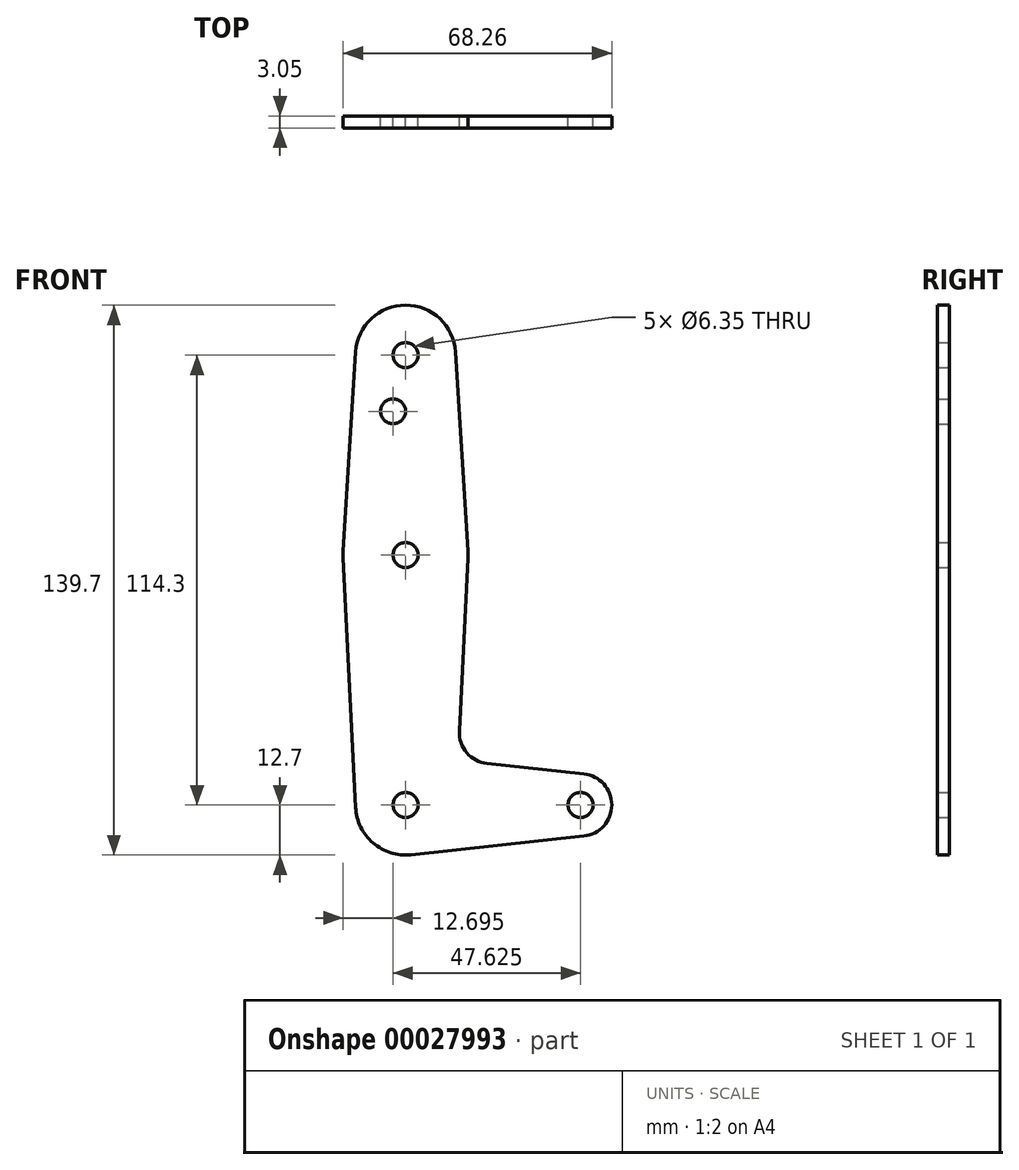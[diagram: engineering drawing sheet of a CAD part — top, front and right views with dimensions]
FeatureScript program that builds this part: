
annotation { "Feature Type Name" : "Feature", "Feature Type Description" : "" }
export const myFeature = defineFeature(function(context is Context, id is Id, definition is map)
    precondition{}
    {
        {
            var Q0;
            Q0=qCreatedBy(makeId("Front.planeOp"),FACE);
            var sketch = newSketch(context, id + "F0", { "sketchPlane" : qUnion([Q0])});
            skLineSegment(sketch, "E0", {"start": v(0, 0) * mm, "end": v(0, 114.3) * mm, "construction": true});
            skLineSegment(sketch, "E1", {"start": v(0, 0) * mm, "end": v(44.45, 0) * mm, "construction": true});
            skCircle(sketch, "E2", {"center": v(0, 0) * mm, "radius": 12.7 * mm});
            skCircle(sketch, "E3", {"center": v(44.45, 0) * mm, "radius": 7.94 * mm});
            skCircle(sketch, "E4", {"center": v(0, 114.3) * mm, "radius": 12.7 * mm});
            skCircle(sketch, "E5", {"center": v(0, 63.5) * mm, "radius": 15.88 * mm});
            skLineSegment(sketch, "E6", {"start": v(-12.68, 115.1) * mm, "end": v(-15.84, 64.5) * mm});
            skLineSegment(sketch, "E7", {"start": v(-15.86, 62.7) * mm, "end": v(-12.68, -0.63) * mm});
            skLineSegment(sketch, "E8", {"start": v(12.68, 115.1) * mm, "end": v(15.84, 64.5) * mm});
            skLineSegment(sketch, "E9", {"start": v(15.86, 62.7) * mm, "end": v(13.66, 18.84) * mm});
            skLineSegment(sketch, "E10", {"start": v(20.75, 10.54) * mm, "end": v(45.3, 7.9) * mm});
            skLineSegment(sketch, "E11", {"start": v(1.36, -12.63) * mm, "end": v(45.3, -7.9) * mm});
            skCircle(sketch, "E12", {"center": v(0, 114.3) * mm, "radius": 3.18 * mm});
            skCircle(sketch, "E13", {"center": v(0, 63.5) * mm, "radius": 3.18 * mm});
            skCircle(sketch, "E14", {"center": v(0, 0) * mm, "radius": 3.18 * mm});
            skCircle(sketch, "E15", {"center": v(44.45, 0) * mm, "radius": 3.18 * mm});
            skCircle(sketch, "E16", {"center": v(-3.18, 100.03) * mm, "radius": 3.18 * mm});
            skArc(sketch, "E17.filletArc", {"start": v(13.66, 18.84) * mm, "mid": v(15.55, 13.28) * mm, "end": v(20.75, 10.54) * mm});
            skSolve(sketch);
        }
        {
            var Q0;
            Q0=makeQuery(id+"F0.imprint","IMPRINT",FACE,{"disambiguationData":[TD([[makeQuery(id+"F0.imprint","IMPRINT",EDGE,{"derivedFrom":sQuery(id+"F0.wireOp",EDGE,"E14")}),-1.0]])]});
            var Q1;
            Q1=makeQuery(id+"F0.imprint","IMPRINT",FACE,{"disambiguationData":[TD([[makeQuery(id+"F0.imprint","IMPRINT",EDGE,{"derivedFrom":sQuery(id+"F0.wireOp",EDGE,"E15")}),-1.0]])]});
            var Q2;
            {var subQ2=sQuery(id+"F0.wireOp",EDGE,"E7");Q2=makeQuery(id+"F0.imprint","IMPRINT",FACE,{"disambiguationData":[TD([[makeQuery(id+"F0.imprint","IMPRINT",EDGE,{"derivedFrom":subQ2}),1.0]])]});}
            var Q3;
            Q3=makeQuery(id+"F0.imprint","IMPRINT",FACE,{"disambiguationData":[TD([[makeQuery(id+"F0.imprint","IMPRINT",EDGE,{"derivedFrom":sQuery(id+"F0.wireOp",EDGE,"E12")}),-1.0]])]});
            var Q4;
            {var subQ1=sQuery(id+"F0.wireOp",EDGE,"E6");Q4=makeQuery(id+"F0.imprint","IMPRINT",FACE,{"disambiguationData":[TD([[makeQuery(id+"F0.imprint","IMPRINT",EDGE,{"derivedFrom":subQ1}),1.0]])]});}
            var Q5;
            Q5=makeQuery(id+"F0.imprint","IMPRINT",FACE,{"disambiguationData":[TD([[makeQuery(id+"F0.imprint","IMPRINT",EDGE,{"derivedFrom":sQuery(id+"F0.wireOp",EDGE,"E13")}),-1.0]])]});
            extrude(context, id + "F1", {"entities" : qUnion([Q0, Q1, Q2, Q3, Q4, Q5]), "depth" : 3.05 * mm});
        }
    });
